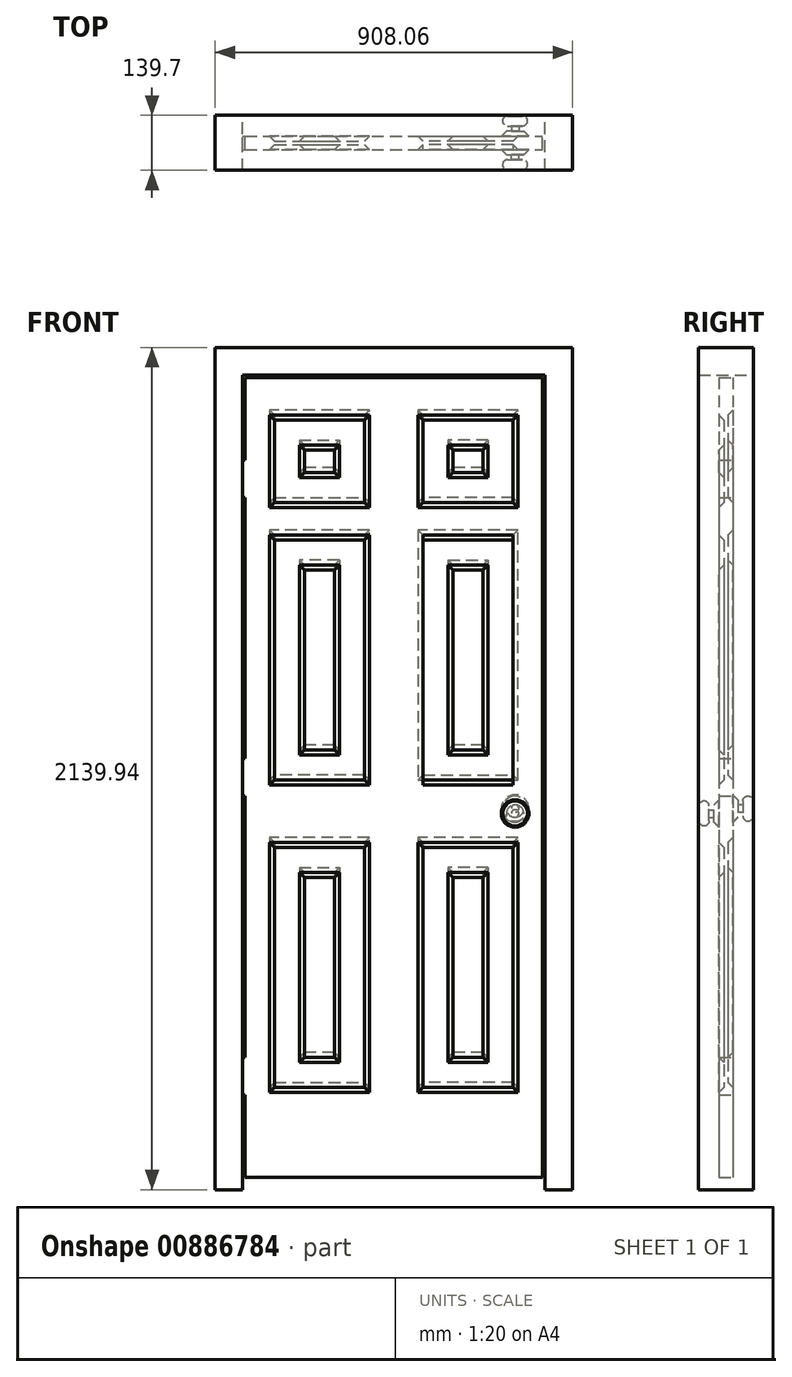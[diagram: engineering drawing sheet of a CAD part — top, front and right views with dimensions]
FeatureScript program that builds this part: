
annotation { "Feature Type Name" : "Feature", "Feature Type Description" : "" }
export const myFeature = defineFeature(function(context is Context, id is Id, definition is map)
    precondition{}
    {
        {
            var Q0;
            Q0=qCreatedBy(makeId("Front.planeOp"),FACE);
            var sketch = newSketch(context, id + "F0", { "sketchPlane" : qUnion([Q0])});
            skLineSegment(sketch, "E0.bottom", {"start": v(-454.03, 1069.98) * mm, "end": v(454.02, 1069.98) * mm});
            skLineSegment(sketch, "E0.top", {"start": v(-454.03, -1069.98) * mm, "end": v(-384.18, -1069.98) * mm});
            skLineSegment(sketch, "E0.left", {"start": v(-454.03, 1069.97) * mm, "end": v(-454.03, -1069.98) * mm});
            skLineSegment(sketch, "E0.right", {"start": v(454.02, 1069.98) * mm, "end": v(454.02, -1069.98) * mm});
            skPoint(sketch, "E0.middle", {"position": v(0, 0) * mm});
            skLineSegment(sketch, "E1.bottom", {"start": v(-384.18, 1000.13) * mm, "end": v(384.17, 1000.13) * mm});
            skLineSegment(sketch, "E1.left", {"start": v(-384.18, 1000.13) * mm, "end": v(-384.18, -1069.98) * mm});
            skLineSegment(sketch, "E1.right", {"start": v(384.17, 1000.13) * mm, "end": v(384.17, -1069.98) * mm});
            skLineSegment(sketch, "E2.trimOffspring", {"start": v(384.17, -1069.98) * mm, "end": v(454.02, -1069.98) * mm});
            skLineSegment(sketch, "E3.bottom", {"start": v(-377.83, 993.78) * mm, "end": v(377.82, 993.78) * mm});
            skLineSegment(sketch, "E3.top", {"start": v(-377.83, -1038.22) * mm, "end": v(377.82, -1038.22) * mm});
            skLineSegment(sketch, "E3.left", {"start": v(-377.83, 993.78) * mm, "end": v(-377.83, 784.23) * mm});
            skLineSegment(sketch, "E3.right", {"start": v(377.82, 993.78) * mm, "end": v(377.82, -1038.22) * mm});
            skLineSegment(sketch, "E4", {"start": v(-384.18, 784.23) * mm, "end": v(-377.83, 784.23) * mm});
            skLineSegment(sketch, "E5", {"start": v(-384.18, 688.98) * mm, "end": v(-377.83, 688.98) * mm});
            skLineSegment(sketch, "E6", {"start": v(-384.18, 25.4) * mm, "end": v(-377.83, 25.4) * mm});
            skLineSegment(sketch, "E7", {"start": v(-384.18, -69.85) * mm, "end": v(-377.83, -69.85) * mm});
            skLineSegment(sketch, "E8", {"start": v(-384.18, -733.42) * mm, "end": v(-377.83, -733.42) * mm});
            skLineSegment(sketch, "E9", {"start": v(-384.18, -828.67) * mm, "end": v(-377.83, -828.67) * mm});
            skLineSegment(sketch, "E10.trimOffspring", {"start": v(-377.83, -828.67) * mm, "end": v(-377.83, -1038.22) * mm});
            skLineSegment(sketch, "E11.trimOffspring", {"start": v(-377.83, -69.85) * mm, "end": v(-377.83, -733.42) * mm});
            skLineSegment(sketch, "E12.trimOffspring", {"start": v(-377.83, 688.98) * mm, "end": v(-377.83, 25.4) * mm});
            skSolve(sketch);
        }
        {
            var Q0;
            Q0=makeQuery(id+"F0.imprint","IMPRINT",FACE,{"disambiguationData":[TD([[makeQuery(id+"F0.imprint","IMPRINT",EDGE,{"derivedFrom":sQuery(id+"F0.wireOp",EDGE,"E0.bottom")}),-1.0]])]});
            extrude(context, id + "F1", {"entities" : qUnion([Q0]), "endBound" : BoundingType.SYMMETRIC, "depth" : 139.7 * mm, "offsetDistance" : 25.4 * mm});
        }
        {
            var Q0;
            Q0=makeQuery(id+"F0.imprint","IMPRINT",FACE,{"disambiguationData":[TD([[makeQuery(id+"F0.imprint","IMPRINT",EDGE,{"derivedFrom":sQuery(id+"F0.wireOp",EDGE,"E3.bottom")}),-1.0]])]});
            extrude(context, id + "F2", {"entities" : qUnion([Q0]), "operationType" : NewBodyOperationType.ADD, "endBound" : BoundingType.SYMMETRIC, "depth" : 34.92 * mm, "offsetDistance" : 25.4 * mm});
        }
        {
            var Q0;
            Q0=makeQuery(id+"F2.opExtrude","CAP_FACE",FACE,{"disambiguationData":[OSD([sQuery(id+"F0.wireOp",EDGE,"E1.left"),sQuery(id+"F0.wireOp",EDGE,"E3.bottom"),sQuery(id+"F0.wireOp",EDGE,"E3.top"),sQuery(id+"F0.wireOp",EDGE,"E3.left"),sQuery(id+"F0.wireOp",EDGE,"E3.right"),sQuery(id+"F0.wireOp",EDGE,"E4"),sQuery(id+"F0.wireOp",EDGE,"E5"),sQuery(id+"F0.wireOp",EDGE,"E6"),sQuery(id+"F0.wireOp",EDGE,"E7"),sQuery(id+"F0.wireOp",EDGE,"E8"),sQuery(id+"F0.wireOp",EDGE,"E9"),sQuery(id+"F0.wireOp",EDGE,"E10.trimOffspring"),sQuery(id+"F0.wireOp",EDGE,"E11.trimOffspring"),sQuery(id+"F0.wireOp",EDGE,"E12.trimOffspring")])],"isStart":false});
            var sketch = newSketch(context, id + "F3", { "sketchPlane" : qUnion([Q0])});
            skLineSegment(sketch, "E13", {"start": v(0, 520.5) * mm, "end": v(0, -306.5) * mm});
            skLineSegment(sketch, "E14.bottom", {"start": v(-303.21, 885.83) * mm, "end": v(-74.61, 885.83) * mm});
            skLineSegment(sketch, "E14.top", {"start": v(-303.21, 676.28) * mm, "end": v(-74.61, 676.28) * mm});
            skLineSegment(sketch, "E14.left", {"start": v(-303.21, 885.83) * mm, "end": v(-303.21, 676.28) * mm});
            skLineSegment(sketch, "E14.right", {"start": v(-74.61, 885.83) * mm, "end": v(-74.61, 676.28) * mm});
            skLineSegment(sketch, "E15.bottom", {"start": v(-74.61, 581.03) * mm, "end": v(-303.21, 581.03) * mm});
            skLineSegment(sketch, "E15.top", {"start": v(-74.61, -28.57) * mm, "end": v(-303.21, -28.57) * mm});
            skLineSegment(sketch, "E15.left", {"start": v(-74.61, 581.03) * mm, "end": v(-74.61, -28.57) * mm});
            skLineSegment(sketch, "E15.right", {"start": v(-303.21, 581.03) * mm, "end": v(-303.21, -28.57) * mm});
            skLineSegment(sketch, "E16.bottom", {"start": v(-303.21, -200.02) * mm, "end": v(-74.61, -200.02) * mm});
            skLineSegment(sketch, "E16.top", {"start": v(-303.21, -809.62) * mm, "end": v(-74.61, -809.62) * mm});
            skLineSegment(sketch, "E16.left", {"start": v(-303.21, -200.02) * mm, "end": v(-303.21, -809.62) * mm});
            skLineSegment(sketch, "E16.right", {"start": v(-74.61, -200.02) * mm, "end": v(-74.61, -809.62) * mm});
            skLineSegment(sketch, "E17.0", {"start": v(-239.71, -263.52) * mm, "end": v(-239.71, -746.12) * mm});
            skLineSegment(sketch, "E17.1", {"start": v(-239.71, -263.52) * mm, "end": v(-138.11, -263.52) * mm});
            skLineSegment(sketch, "E17.2", {"start": v(-138.11, -263.52) * mm, "end": v(-138.11, -746.12) * mm});
            skLineSegment(sketch, "E17.3", {"start": v(-239.71, -746.12) * mm, "end": v(-138.11, -746.12) * mm});
            skLineSegment(sketch, "E18.0", {"start": v(-239.71, 517.53) * mm, "end": v(-239.71, 34.93) * mm});
            skLineSegment(sketch, "E18.1", {"start": v(-138.11, 517.53) * mm, "end": v(-239.71, 517.53) * mm});
            skLineSegment(sketch, "E18.2", {"start": v(-138.11, 517.53) * mm, "end": v(-138.11, 34.93) * mm});
            skLineSegment(sketch, "E18.3", {"start": v(-138.11, 34.93) * mm, "end": v(-239.71, 34.93) * mm});
            skLineSegment(sketch, "E19.0", {"start": v(-239.71, 822.33) * mm, "end": v(-239.71, 739.78) * mm});
            skLineSegment(sketch, "E19.1", {"start": v(-239.71, 822.33) * mm, "end": v(-138.11, 822.33) * mm});
            skLineSegment(sketch, "E19.2", {"start": v(-138.11, 822.33) * mm, "end": v(-138.11, 739.78) * mm});
            skLineSegment(sketch, "E19.3", {"start": v(-239.71, 739.78) * mm, "end": v(-138.11, 739.78) * mm});
            skLineSegment(sketch, "E20.MirrorCS", {"start": v(239.71, 822.33) * mm, "end": v(239.71, 739.78) * mm});
            skLineSegment(sketch, "E21.MirrorCS", {"start": v(138.11, 822.33) * mm, "end": v(138.11, 739.78) * mm});
            skLineSegment(sketch, "E22.MirrorCS", {"start": v(74.61, 885.83) * mm, "end": v(74.61, 676.28) * mm});
            skLineSegment(sketch, "E23.MirrorCS", {"start": v(303.21, 885.83) * mm, "end": v(74.61, 885.83) * mm});
            skLineSegment(sketch, "E24.MirrorCS", {"start": v(303.21, 676.28) * mm, "end": v(74.61, 676.28) * mm});
            skLineSegment(sketch, "E25.MirrorCS", {"start": v(303.21, 581.03) * mm, "end": v(303.21, -28.57) * mm});
            skLineSegment(sketch, "E26.MirrorCS", {"start": v(239.71, 517.53) * mm, "end": v(239.71, 34.93) * mm});
            skLineSegment(sketch, "E27.MirrorCS", {"start": v(138.11, 34.93) * mm, "end": v(239.71, 34.93) * mm});
            skLineSegment(sketch, "E28.MirrorCS", {"start": v(74.61, 581.03) * mm, "end": v(74.61, -28.57) * mm});
            skLineSegment(sketch, "E29.MirrorCS", {"start": v(303.21, -809.62) * mm, "end": v(74.61, -809.62) * mm});
            skLineSegment(sketch, "E30.MirrorCS", {"start": v(138.11, 517.53) * mm, "end": v(239.71, 517.53) * mm});
            skLineSegment(sketch, "E31.MirrorCS", {"start": v(74.61, -28.57) * mm, "end": v(303.21, -28.57) * mm});
            skLineSegment(sketch, "E32.MirrorCS", {"start": v(239.71, 822.33) * mm, "end": v(138.11, 822.33) * mm});
            skLineSegment(sketch, "E33.MirrorCS", {"start": v(239.71, -263.52) * mm, "end": v(138.11, -263.52) * mm});
            skLineSegment(sketch, "E34.MirrorCS", {"start": v(239.71, 739.78) * mm, "end": v(138.11, 739.78) * mm});
            skLineSegment(sketch, "E35.MirrorCS", {"start": v(303.21, 885.83) * mm, "end": v(303.21, 676.28) * mm});
            skLineSegment(sketch, "E36.MirrorCS", {"start": v(303.21, -200.02) * mm, "end": v(74.61, -200.02) * mm});
            skLineSegment(sketch, "E37.MirrorCS", {"start": v(138.11, 517.53) * mm, "end": v(138.11, 34.93) * mm});
            skLineSegment(sketch, "E38.MirrorCS", {"start": v(239.71, -746.12) * mm, "end": v(138.11, -746.12) * mm});
            skLineSegment(sketch, "E39.MirrorCS", {"start": v(138.11, -263.52) * mm, "end": v(138.11, -746.12) * mm});
            skLineSegment(sketch, "E40.MirrorCS", {"start": v(303.21, -200.02) * mm, "end": v(303.21, -809.62) * mm});
            skLineSegment(sketch, "E41.MirrorCS", {"start": v(74.61, 581.03) * mm, "end": v(303.21, 581.03) * mm});
            skLineSegment(sketch, "E42.MirrorCS", {"start": v(74.61, -200.02) * mm, "end": v(74.61, -809.62) * mm});
            skLineSegment(sketch, "E43.MirrorCS", {"start": v(239.71, -263.52) * mm, "end": v(239.71, -746.12) * mm});
            skSolve(sketch);
        }
        {
            var Q0;
            Q0=makeQuery(id+"F3.imprint","IMPRINT",FACE,{"disambiguationData":[TD([[makeQuery(id+"F3.imprint","IMPRINT",EDGE,{"derivedFrom":sQuery(id+"F3.wireOp",EDGE,"E14.bottom")}),-1.0]])]});
            var Q1;
            Q1=makeQuery(id+"F3.imprint","IMPRINT",FACE,{"disambiguationData":[TD([[makeQuery(id+"F3.imprint","IMPRINT",EDGE,{"derivedFrom":sQuery(id+"F3.wireOp",EDGE,"E15.bottom")}),1.0]])]});
            var Q2;
            Q2=makeQuery(id+"F3.imprint","IMPRINT",FACE,{"disambiguationData":[TD([[makeQuery(id+"F3.imprint","IMPRINT",EDGE,{"derivedFrom":sQuery(id+"F3.wireOp",EDGE,"E20.MirrorCS")}),1.0]])]});
            var Q3;
            Q3=makeQuery(id+"F3.imprint","IMPRINT",FACE,{"disambiguationData":[TD([[makeQuery(id+"F3.imprint","IMPRINT",EDGE,{"derivedFrom":sQuery(id+"F3.wireOp",EDGE,"E25.MirrorCS")}),-1.0]])]});
            var Q4;
            Q4=makeQuery(id+"F3.imprint","IMPRINT",FACE,{"disambiguationData":[TD([[makeQuery(id+"F3.imprint","IMPRINT",EDGE,{"derivedFrom":sQuery(id+"F3.wireOp",EDGE,"E16.bottom")}),-1.0]])]});
            var Q5;
            Q5=makeQuery(id+"F3.imprint","IMPRINT",FACE,{"disambiguationData":[TD([[makeQuery(id+"F3.imprint","IMPRINT",EDGE,{"derivedFrom":sQuery(id+"F3.wireOp",EDGE,"E29.MirrorCS")}),-1.0]])]});
            extrude(context, id + "F4", {"entities" : qUnion([Q0, Q1, Q2, Q3, Q4, Q5]), "operationType" : NewBodyOperationType.REMOVE, "oppositeDirection" : true, "depth" : 12.7 * mm, "offsetDistance" : 25.4 * mm});
        }
        {
            var Q0;
            Q0=makeQuery(id+"F4.boolean.opBoolean","SPLIT",FACE,{"disambiguationData":[TD([makeQuery(id+"F4.opExtrude","SWEPT_FACE",FACE,{"disambiguationData":[OSD([sQuery(id+"F3.wireOp",EDGE,"E18.0")])]})])],"derivedFrom":makeQuery(id+"F2.opExtrude","CAP_FACE",FACE,{"disambiguationData":[OSD([sQuery(id+"F0.wireOp",EDGE,"E1.left"),sQuery(id+"F0.wireOp",EDGE,"E3.bottom"),sQuery(id+"F0.wireOp",EDGE,"E3.top"),sQuery(id+"F0.wireOp",EDGE,"E3.left"),sQuery(id+"F0.wireOp",EDGE,"E3.right"),sQuery(id+"F0.wireOp",EDGE,"E4"),sQuery(id+"F0.wireOp",EDGE,"E5"),sQuery(id+"F0.wireOp",EDGE,"E6"),sQuery(id+"F0.wireOp",EDGE,"E7"),sQuery(id+"F0.wireOp",EDGE,"E8"),sQuery(id+"F0.wireOp",EDGE,"E9"),sQuery(id+"F0.wireOp",EDGE,"E10.trimOffspring"),sQuery(id+"F0.wireOp",EDGE,"E11.trimOffspring"),sQuery(id+"F0.wireOp",EDGE,"E12.trimOffspring")])],"isStart":false})});
            var Q1;
            Q1=makeQuery(id+"F4.boolean.opBoolean","SPLIT",FACE,{"disambiguationData":[TD([makeQuery(id+"F4.opExtrude","SWEPT_FACE",FACE,{"disambiguationData":[OSD([sQuery(id+"F3.wireOp",EDGE,"E19.0")])]})])],"derivedFrom":makeQuery(id+"F2.opExtrude","CAP_FACE",FACE,{"disambiguationData":[OSD([sQuery(id+"F0.wireOp",EDGE,"E1.left"),sQuery(id+"F0.wireOp",EDGE,"E3.bottom"),sQuery(id+"F0.wireOp",EDGE,"E3.top"),sQuery(id+"F0.wireOp",EDGE,"E3.left"),sQuery(id+"F0.wireOp",EDGE,"E3.right"),sQuery(id+"F0.wireOp",EDGE,"E4"),sQuery(id+"F0.wireOp",EDGE,"E5"),sQuery(id+"F0.wireOp",EDGE,"E6"),sQuery(id+"F0.wireOp",EDGE,"E7"),sQuery(id+"F0.wireOp",EDGE,"E8"),sQuery(id+"F0.wireOp",EDGE,"E9"),sQuery(id+"F0.wireOp",EDGE,"E10.trimOffspring"),sQuery(id+"F0.wireOp",EDGE,"E11.trimOffspring"),sQuery(id+"F0.wireOp",EDGE,"E12.trimOffspring")])],"isStart":false})});
            var Q2;
            Q2=makeQuery(id+"F4.boolean.opBoolean","SPLIT",FACE,{"disambiguationData":[TD([makeQuery(id+"F4.opExtrude","SWEPT_FACE",FACE,{"disambiguationData":[OSD([sQuery(id+"F3.wireOp",EDGE,"E20.MirrorCS")])]})])],"derivedFrom":makeQuery(id+"F2.opExtrude","CAP_FACE",FACE,{"disambiguationData":[OSD([sQuery(id+"F0.wireOp",EDGE,"E1.left"),sQuery(id+"F0.wireOp",EDGE,"E3.bottom"),sQuery(id+"F0.wireOp",EDGE,"E3.top"),sQuery(id+"F0.wireOp",EDGE,"E3.left"),sQuery(id+"F0.wireOp",EDGE,"E3.right"),sQuery(id+"F0.wireOp",EDGE,"E4"),sQuery(id+"F0.wireOp",EDGE,"E5"),sQuery(id+"F0.wireOp",EDGE,"E6"),sQuery(id+"F0.wireOp",EDGE,"E7"),sQuery(id+"F0.wireOp",EDGE,"E8"),sQuery(id+"F0.wireOp",EDGE,"E9"),sQuery(id+"F0.wireOp",EDGE,"E10.trimOffspring"),sQuery(id+"F0.wireOp",EDGE,"E11.trimOffspring"),sQuery(id+"F0.wireOp",EDGE,"E12.trimOffspring")])],"isStart":false})});
            var Q3;
            Q3=makeQuery(id+"F4.boolean.opBoolean","SPLIT",FACE,{"disambiguationData":[TD([makeQuery(id+"F4.opExtrude","SWEPT_FACE",FACE,{"disambiguationData":[OSD([sQuery(id+"F3.wireOp",EDGE,"E26.MirrorCS")])]})])],"derivedFrom":makeQuery(id+"F2.opExtrude","CAP_FACE",FACE,{"disambiguationData":[OSD([sQuery(id+"F0.wireOp",EDGE,"E1.left"),sQuery(id+"F0.wireOp",EDGE,"E3.bottom"),sQuery(id+"F0.wireOp",EDGE,"E3.top"),sQuery(id+"F0.wireOp",EDGE,"E3.left"),sQuery(id+"F0.wireOp",EDGE,"E3.right"),sQuery(id+"F0.wireOp",EDGE,"E4"),sQuery(id+"F0.wireOp",EDGE,"E5"),sQuery(id+"F0.wireOp",EDGE,"E6"),sQuery(id+"F0.wireOp",EDGE,"E7"),sQuery(id+"F0.wireOp",EDGE,"E8"),sQuery(id+"F0.wireOp",EDGE,"E9"),sQuery(id+"F0.wireOp",EDGE,"E10.trimOffspring"),sQuery(id+"F0.wireOp",EDGE,"E11.trimOffspring"),sQuery(id+"F0.wireOp",EDGE,"E12.trimOffspring")])],"isStart":false})});
            var Q4;
            Q4=makeQuery(id+"F4.boolean.opBoolean","SPLIT",FACE,{"disambiguationData":[TD([makeQuery(id+"F4.opExtrude","SWEPT_FACE",FACE,{"disambiguationData":[OSD([sQuery(id+"F3.wireOp",EDGE,"E17.0")])]})])],"derivedFrom":makeQuery(id+"F2.opExtrude","CAP_FACE",FACE,{"disambiguationData":[OSD([sQuery(id+"F0.wireOp",EDGE,"E1.left"),sQuery(id+"F0.wireOp",EDGE,"E3.bottom"),sQuery(id+"F0.wireOp",EDGE,"E3.top"),sQuery(id+"F0.wireOp",EDGE,"E3.left"),sQuery(id+"F0.wireOp",EDGE,"E3.right"),sQuery(id+"F0.wireOp",EDGE,"E4"),sQuery(id+"F0.wireOp",EDGE,"E5"),sQuery(id+"F0.wireOp",EDGE,"E6"),sQuery(id+"F0.wireOp",EDGE,"E7"),sQuery(id+"F0.wireOp",EDGE,"E8"),sQuery(id+"F0.wireOp",EDGE,"E9"),sQuery(id+"F0.wireOp",EDGE,"E10.trimOffspring"),sQuery(id+"F0.wireOp",EDGE,"E11.trimOffspring"),sQuery(id+"F0.wireOp",EDGE,"E12.trimOffspring")])],"isStart":false})});
            var Q5;
            Q5=makeQuery(id+"F4.boolean.opBoolean","SPLIT",FACE,{"disambiguationData":[TD([makeQuery(id+"F4.opExtrude","SWEPT_FACE",FACE,{"disambiguationData":[OSD([sQuery(id+"F3.wireOp",EDGE,"E33.MirrorCS")])]})])],"derivedFrom":makeQuery(id+"F2.opExtrude","CAP_FACE",FACE,{"disambiguationData":[OSD([sQuery(id+"F0.wireOp",EDGE,"E1.left"),sQuery(id+"F0.wireOp",EDGE,"E3.bottom"),sQuery(id+"F0.wireOp",EDGE,"E3.top"),sQuery(id+"F0.wireOp",EDGE,"E3.left"),sQuery(id+"F0.wireOp",EDGE,"E3.right"),sQuery(id+"F0.wireOp",EDGE,"E4"),sQuery(id+"F0.wireOp",EDGE,"E5"),sQuery(id+"F0.wireOp",EDGE,"E6"),sQuery(id+"F0.wireOp",EDGE,"E7"),sQuery(id+"F0.wireOp",EDGE,"E8"),sQuery(id+"F0.wireOp",EDGE,"E9"),sQuery(id+"F0.wireOp",EDGE,"E10.trimOffspring"),sQuery(id+"F0.wireOp",EDGE,"E11.trimOffspring"),sQuery(id+"F0.wireOp",EDGE,"E12.trimOffspring")])],"isStart":false})});
            var Q6;
            Q6=makeQuery(id+"F4.boolean.opBoolean","COPY",EDGE,{"derivedFrom":makeQuery(id+"F4.opExtrude","CAP_EDGE",EDGE,{"disambiguationData":[OSD([sQuery(id+"F3.wireOp",EDGE,"E14.left")])],"isStart":true})});
            var Q7;
            Q7=makeQuery(id+"F4.boolean.opBoolean","COPY",EDGE,{"derivedFrom":makeQuery(id+"F4.opExtrude","CAP_EDGE",EDGE,{"disambiguationData":[OSD([sQuery(id+"F3.wireOp",EDGE,"E14.bottom")])],"isStart":true})});
            var Q8;
            Q8=makeQuery(id+"F4.boolean.opBoolean","COPY",EDGE,{"derivedFrom":makeQuery(id+"F4.opExtrude","CAP_EDGE",EDGE,{"disambiguationData":[OSD([sQuery(id+"F3.wireOp",EDGE,"E14.right")])],"isStart":true})});
            var Q9;
            Q9=makeQuery(id+"F4.boolean.opBoolean","COPY",EDGE,{"derivedFrom":makeQuery(id+"F4.opExtrude","CAP_EDGE",EDGE,{"disambiguationData":[OSD([sQuery(id+"F3.wireOp",EDGE,"E14.top")])],"isStart":true})});
            var Q10;
            Q10=makeQuery(id+"F4.boolean.opBoolean","COPY",EDGE,{"derivedFrom":makeQuery(id+"F4.opExtrude","CAP_EDGE",EDGE,{"disambiguationData":[OSD([sQuery(id+"F3.wireOp",EDGE,"E15.bottom")])],"isStart":true})});
            var Q11;
            Q11=makeQuery(id+"F4.boolean.opBoolean","COPY",EDGE,{"derivedFrom":makeQuery(id+"F4.opExtrude","CAP_EDGE",EDGE,{"disambiguationData":[OSD([sQuery(id+"F3.wireOp",EDGE,"E15.right")])],"isStart":true})});
            var Q12;
            Q12=makeQuery(id+"F4.boolean.opBoolean","COPY",EDGE,{"derivedFrom":makeQuery(id+"F4.opExtrude","CAP_EDGE",EDGE,{"disambiguationData":[OSD([sQuery(id+"F3.wireOp",EDGE,"E15.left")])],"isStart":true})});
            var Q13;
            Q13=makeQuery(id+"F4.boolean.opBoolean","COPY",EDGE,{"derivedFrom":makeQuery(id+"F4.opExtrude","CAP_EDGE",EDGE,{"disambiguationData":[OSD([sQuery(id+"F3.wireOp",EDGE,"E22.MirrorCS")])],"isStart":true})});
            var Q14;
            Q14=makeQuery(id+"F4.boolean.opBoolean","COPY",EDGE,{"derivedFrom":makeQuery(id+"F4.opExtrude","CAP_EDGE",EDGE,{"disambiguationData":[OSD([sQuery(id+"F3.wireOp",EDGE,"E23.MirrorCS")])],"isStart":true})});
            var Q15;
            Q15=makeQuery(id+"F4.boolean.opBoolean","COPY",EDGE,{"derivedFrom":makeQuery(id+"F4.opExtrude","CAP_EDGE",EDGE,{"disambiguationData":[OSD([sQuery(id+"F3.wireOp",EDGE,"E35.MirrorCS")])],"isStart":true})});
            var Q16;
            Q16=makeQuery(id+"F4.boolean.opBoolean","COPY",EDGE,{"derivedFrom":makeQuery(id+"F4.opExtrude","CAP_EDGE",EDGE,{"disambiguationData":[OSD([sQuery(id+"F3.wireOp",EDGE,"E24.MirrorCS")])],"isStart":true})});
            var Q17;
            Q17=makeQuery(id+"F4.boolean.opBoolean","COPY",EDGE,{"derivedFrom":makeQuery(id+"F4.opExtrude","CAP_EDGE",EDGE,{"disambiguationData":[OSD([sQuery(id+"F3.wireOp",EDGE,"E41.MirrorCS")])],"isStart":true})});
            var Q18;
            Q18=makeQuery(id+"F4.boolean.opBoolean","COPY",EDGE,{"derivedFrom":makeQuery(id+"F4.opExtrude","CAP_EDGE",EDGE,{"disambiguationData":[OSD([sQuery(id+"F3.wireOp",EDGE,"E15.top")])],"isStart":true})});
            var Q19;
            Q19=makeQuery(id+"F4.boolean.opBoolean","COPY",EDGE,{"derivedFrom":makeQuery(id+"F4.opExtrude","CAP_EDGE",EDGE,{"disambiguationData":[OSD([sQuery(id+"F3.wireOp",EDGE,"E31.MirrorCS")])],"isStart":true})});
            var Q20;
            Q20=makeQuery(id+"F4.boolean.opBoolean","COPY",EDGE,{"derivedFrom":makeQuery(id+"F4.opExtrude","CAP_EDGE",EDGE,{"disambiguationData":[OSD([sQuery(id+"F3.wireOp",EDGE,"E16.bottom")])],"isStart":true})});
            var Q21;
            Q21=makeQuery(id+"F4.boolean.opBoolean","COPY",EDGE,{"derivedFrom":makeQuery(id+"F4.opExtrude","CAP_EDGE",EDGE,{"disambiguationData":[OSD([sQuery(id+"F3.wireOp",EDGE,"E16.left")])],"isStart":true})});
            var Q22;
            Q22=makeQuery(id+"F4.boolean.opBoolean","COPY",EDGE,{"derivedFrom":makeQuery(id+"F4.opExtrude","CAP_EDGE",EDGE,{"disambiguationData":[OSD([sQuery(id+"F3.wireOp",EDGE,"E16.right")])],"isStart":true})});
            var Q23;
            Q23=makeQuery(id+"F4.boolean.opBoolean","COPY",EDGE,{"derivedFrom":makeQuery(id+"F4.opExtrude","CAP_EDGE",EDGE,{"disambiguationData":[OSD([sQuery(id+"F3.wireOp",EDGE,"E36.MirrorCS")])],"isStart":true})});
            var Q24;
            Q24=makeQuery(id+"F4.boolean.opBoolean","COPY",EDGE,{"derivedFrom":makeQuery(id+"F4.opExtrude","CAP_EDGE",EDGE,{"disambiguationData":[OSD([sQuery(id+"F3.wireOp",EDGE,"E42.MirrorCS")])],"isStart":true})});
            var Q25;
            Q25=makeQuery(id+"F4.boolean.opBoolean","COPY",EDGE,{"derivedFrom":makeQuery(id+"F4.opExtrude","CAP_EDGE",EDGE,{"disambiguationData":[OSD([sQuery(id+"F3.wireOp",EDGE,"E40.MirrorCS")])],"isStart":true})});
            var Q26;
            Q26=makeQuery(id+"F4.boolean.opBoolean","COPY",EDGE,{"derivedFrom":makeQuery(id+"F4.opExtrude","CAP_EDGE",EDGE,{"disambiguationData":[OSD([sQuery(id+"F3.wireOp",EDGE,"E16.top")])],"isStart":true})});
            var Q27;
            Q27=makeQuery(id+"F4.boolean.opBoolean","COPY",EDGE,{"derivedFrom":makeQuery(id+"F4.opExtrude","CAP_EDGE",EDGE,{"disambiguationData":[OSD([sQuery(id+"F3.wireOp",EDGE,"E29.MirrorCS")])],"isStart":true})});
            chamfer(context, id + "F5", {"entities" : qUnion([Q0, Q1, Q2, Q3, Q4, Q5, Q6, Q7, Q8, Q9, Q10, Q11, Q12, Q13, Q14, Q15, Q16, Q17, Q18, Q19, Q20, Q21, Q22, Q23, Q24, Q25, Q26, Q27]), "width" : 12.7 * mm, "tangentPropagation" : true});
        }
        {
            var Q0;
            Q0=makeQuery(id+"F2.opExtrude","CAP_FACE",FACE,{"disambiguationData":[OSD([sQuery(id+"F0.wireOp",EDGE,"E1.left"),sQuery(id+"F0.wireOp",EDGE,"E3.bottom"),sQuery(id+"F0.wireOp",EDGE,"E3.top"),sQuery(id+"F0.wireOp",EDGE,"E3.left"),sQuery(id+"F0.wireOp",EDGE,"E3.right"),sQuery(id+"F0.wireOp",EDGE,"E4"),sQuery(id+"F0.wireOp",EDGE,"E5"),sQuery(id+"F0.wireOp",EDGE,"E6"),sQuery(id+"F0.wireOp",EDGE,"E7"),sQuery(id+"F0.wireOp",EDGE,"E8"),sQuery(id+"F0.wireOp",EDGE,"E9"),sQuery(id+"F0.wireOp",EDGE,"E10.trimOffspring"),sQuery(id+"F0.wireOp",EDGE,"E11.trimOffspring"),sQuery(id+"F0.wireOp",EDGE,"E12.trimOffspring")])],"isStart":true});
            var sketch = newSketch(context, id + "F6", { "sketchPlane" : qUnion([Q0])});
            skLineSegment(sketch, "E44", {"start": v(0.45, 315.7) * mm, "end": v(0.45, -511.3) * mm});
            skLineSegment(sketch, "E45.bottom", {"start": v(-302.76, 898.53) * mm, "end": v(-74.16, 898.53) * mm});
            skLineSegment(sketch, "E45.top", {"start": v(-302.76, 688.98) * mm, "end": v(-74.16, 688.98) * mm});
            skLineSegment(sketch, "E45.left", {"start": v(-302.76, 898.53) * mm, "end": v(-302.76, 688.98) * mm});
            skLineSegment(sketch, "E45.right", {"start": v(-74.16, 898.53) * mm, "end": v(-74.16, 688.98) * mm});
            skLineSegment(sketch, "E46.bottom", {"start": v(-74.16, 593.73) * mm, "end": v(-302.76, 593.73) * mm});
            skLineSegment(sketch, "E46.top", {"start": v(-74.16, -15.87) * mm, "end": v(-302.76, -15.87) * mm});
            skLineSegment(sketch, "E46.left", {"start": v(-74.16, 593.73) * mm, "end": v(-74.16, -15.87) * mm});
            skLineSegment(sketch, "E46.right", {"start": v(-302.76, 593.73) * mm, "end": v(-302.76, -15.87) * mm});
            skLineSegment(sketch, "E47.bottom", {"start": v(-302.76, -187.32) * mm, "end": v(-74.16, -187.32) * mm});
            skLineSegment(sketch, "E47.top", {"start": v(-302.76, -796.92) * mm, "end": v(-74.16, -796.92) * mm});
            skLineSegment(sketch, "E47.left", {"start": v(-302.76, -187.32) * mm, "end": v(-302.76, -796.92) * mm});
            skLineSegment(sketch, "E47.right", {"start": v(-74.16, -187.32) * mm, "end": v(-74.16, -796.92) * mm});
            skLineSegment(sketch, "E48.0", {"start": v(-239.26, -250.82) * mm, "end": v(-239.26, -733.42) * mm});
            skLineSegment(sketch, "E48.1", {"start": v(-239.26, -250.82) * mm, "end": v(-137.66, -250.82) * mm});
            skLineSegment(sketch, "E48.2", {"start": v(-137.66, -250.82) * mm, "end": v(-137.66, -733.42) * mm});
            skLineSegment(sketch, "E48.3", {"start": v(-239.26, -733.42) * mm, "end": v(-137.66, -733.42) * mm});
            skLineSegment(sketch, "E49.0", {"start": v(-239.26, 530.23) * mm, "end": v(-239.26, 47.63) * mm});
            skLineSegment(sketch, "E49.1", {"start": v(-137.66, 530.23) * mm, "end": v(-239.26, 530.23) * mm});
            skLineSegment(sketch, "E49.2", {"start": v(-137.66, 530.23) * mm, "end": v(-137.66, 47.63) * mm});
            skLineSegment(sketch, "E49.3", {"start": v(-137.66, 47.63) * mm, "end": v(-239.26, 47.63) * mm});
            skLineSegment(sketch, "E50.0", {"start": v(-239.26, 835.03) * mm, "end": v(-239.26, 752.48) * mm});
            skLineSegment(sketch, "E50.1", {"start": v(-239.26, 835.03) * mm, "end": v(-137.66, 835.03) * mm});
            skLineSegment(sketch, "E50.2", {"start": v(-137.66, 835.03) * mm, "end": v(-137.66, 752.48) * mm});
            skLineSegment(sketch, "E50.3", {"start": v(-239.26, 752.48) * mm, "end": v(-137.66, 752.48) * mm});
            skLineSegment(sketch, "E51.MirrorCS", {"start": v(240.16, 835.03) * mm, "end": v(240.16, 752.48) * mm});
            skLineSegment(sketch, "E52.MirrorCS", {"start": v(138.56, 835.03) * mm, "end": v(138.56, 752.48) * mm});
            skLineSegment(sketch, "E53.MirrorCS", {"start": v(75.06, 898.53) * mm, "end": v(75.06, 688.98) * mm});
            skLineSegment(sketch, "E54.MirrorCS", {"start": v(303.66, 898.53) * mm, "end": v(75.06, 898.53) * mm});
            skLineSegment(sketch, "E55.MirrorCS", {"start": v(303.66, 688.98) * mm, "end": v(75.06, 688.98) * mm});
            skLineSegment(sketch, "E56.MirrorCS", {"start": v(303.66, 593.73) * mm, "end": v(303.66, -15.87) * mm});
            skLineSegment(sketch, "E57.MirrorCS", {"start": v(240.16, 530.23) * mm, "end": v(240.16, 47.63) * mm});
            skLineSegment(sketch, "E58.MirrorCS", {"start": v(138.56, 47.63) * mm, "end": v(240.16, 47.63) * mm});
            skLineSegment(sketch, "E59.MirrorCS", {"start": v(75.06, 593.73) * mm, "end": v(75.06, -15.87) * mm});
            skLineSegment(sketch, "E60.MirrorCS", {"start": v(303.66, -796.92) * mm, "end": v(75.06, -796.92) * mm});
            skLineSegment(sketch, "E61.MirrorCS", {"start": v(138.56, 530.23) * mm, "end": v(240.16, 530.23) * mm});
            skLineSegment(sketch, "E62.MirrorCS", {"start": v(75.06, -15.87) * mm, "end": v(303.66, -15.87) * mm});
            skLineSegment(sketch, "E63.MirrorCS", {"start": v(240.16, 835.03) * mm, "end": v(138.56, 835.03) * mm});
            skLineSegment(sketch, "E64.MirrorCS", {"start": v(240.16, -250.82) * mm, "end": v(138.56, -250.82) * mm});
            skLineSegment(sketch, "E65.MirrorCS", {"start": v(240.16, 752.48) * mm, "end": v(138.56, 752.48) * mm});
            skLineSegment(sketch, "E66.MirrorCS", {"start": v(303.66, 898.53) * mm, "end": v(303.66, 688.98) * mm});
            skLineSegment(sketch, "E67.MirrorCS", {"start": v(303.66, -187.32) * mm, "end": v(75.06, -187.32) * mm});
            skLineSegment(sketch, "E68.MirrorCS", {"start": v(138.56, 530.23) * mm, "end": v(138.56, 47.63) * mm});
            skLineSegment(sketch, "E69.MirrorCS", {"start": v(240.16, -733.42) * mm, "end": v(138.56, -733.42) * mm});
            skLineSegment(sketch, "E70.MirrorCS", {"start": v(138.56, -250.82) * mm, "end": v(138.56, -733.42) * mm});
            skLineSegment(sketch, "E71.MirrorCS", {"start": v(303.66, -187.32) * mm, "end": v(303.66, -796.92) * mm});
            skLineSegment(sketch, "E72.MirrorCS", {"start": v(75.06, 593.73) * mm, "end": v(303.66, 593.73) * mm});
            skLineSegment(sketch, "E73.MirrorCS", {"start": v(75.06, -187.32) * mm, "end": v(75.06, -796.92) * mm});
            skLineSegment(sketch, "E74.MirrorCS", {"start": v(240.16, -250.82) * mm, "end": v(240.16, -733.42) * mm});
            skSolve(sketch);
        }
        {
            var Q0;
            Q0=makeQuery(id+"F6.imprint","IMPRINT",FACE,{"disambiguationData":[TD([[makeQuery(id+"F6.imprint","IMPRINT",EDGE,{"derivedFrom":sQuery(id+"F6.wireOp",EDGE,"E45.bottom")}),-1.0]])]});
            var Q1;
            Q1=makeQuery(id+"F6.imprint","IMPRINT",FACE,{"disambiguationData":[TD([[makeQuery(id+"F6.imprint","IMPRINT",EDGE,{"derivedFrom":sQuery(id+"F6.wireOp",EDGE,"E51.MirrorCS")}),1.0]])]});
            var Q2;
            Q2=makeQuery(id+"F6.imprint","IMPRINT",FACE,{"disambiguationData":[TD([[makeQuery(id+"F6.imprint","IMPRINT",EDGE,{"derivedFrom":sQuery(id+"F6.wireOp",EDGE,"E46.bottom")}),1.0]])]});
            var Q3;
            Q3=makeQuery(id+"F6.imprint","IMPRINT",FACE,{"disambiguationData":[TD([[makeQuery(id+"F6.imprint","IMPRINT",EDGE,{"derivedFrom":sQuery(id+"F6.wireOp",EDGE,"E56.MirrorCS")}),-1.0]])]});
            var Q4;
            Q4=makeQuery(id+"F6.imprint","IMPRINT",FACE,{"disambiguationData":[TD([[makeQuery(id+"F6.imprint","IMPRINT",EDGE,{"derivedFrom":sQuery(id+"F6.wireOp",EDGE,"E60.MirrorCS")}),-1.0]])]});
            var Q5;
            Q5=makeQuery(id+"F6.imprint","IMPRINT",FACE,{"disambiguationData":[TD([[makeQuery(id+"F6.imprint","IMPRINT",EDGE,{"derivedFrom":sQuery(id+"F6.wireOp",EDGE,"E47.bottom")}),-1.0]])]});
            extrude(context, id + "F7", {"entities" : qUnion([Q0, Q1, Q2, Q3, Q4, Q5]), "operationType" : NewBodyOperationType.REMOVE, "oppositeDirection" : true, "depth" : 12.7 * mm, "offsetDistance" : 25.4 * mm});
        }
        {
            var Q0;
            Q0=makeQuery(id+"F7.boolean.opBoolean","SPLIT",FACE,{"disambiguationData":[TD([makeQuery(id+"F7.opExtrude","SWEPT_FACE",FACE,{"disambiguationData":[OSD([sQuery(id+"F6.wireOp",EDGE,"E50.0")])]})])],"derivedFrom":makeQuery(id+"F2.opExtrude","CAP_FACE",FACE,{"disambiguationData":[OSD([sQuery(id+"F0.wireOp",EDGE,"E1.left"),sQuery(id+"F0.wireOp",EDGE,"E3.bottom"),sQuery(id+"F0.wireOp",EDGE,"E3.top"),sQuery(id+"F0.wireOp",EDGE,"E3.left"),sQuery(id+"F0.wireOp",EDGE,"E3.right"),sQuery(id+"F0.wireOp",EDGE,"E4"),sQuery(id+"F0.wireOp",EDGE,"E5"),sQuery(id+"F0.wireOp",EDGE,"E6"),sQuery(id+"F0.wireOp",EDGE,"E7"),sQuery(id+"F0.wireOp",EDGE,"E8"),sQuery(id+"F0.wireOp",EDGE,"E9"),sQuery(id+"F0.wireOp",EDGE,"E10.trimOffspring"),sQuery(id+"F0.wireOp",EDGE,"E11.trimOffspring"),sQuery(id+"F0.wireOp",EDGE,"E12.trimOffspring")])],"isStart":true})});
            var Q1;
            Q1=makeQuery(id+"F7.boolean.opBoolean","SPLIT",FACE,{"disambiguationData":[TD([makeQuery(id+"F7.opExtrude","SWEPT_FACE",FACE,{"disambiguationData":[OSD([sQuery(id+"F6.wireOp",EDGE,"E51.MirrorCS")])]})])],"derivedFrom":makeQuery(id+"F2.opExtrude","CAP_FACE",FACE,{"disambiguationData":[OSD([sQuery(id+"F0.wireOp",EDGE,"E1.left"),sQuery(id+"F0.wireOp",EDGE,"E3.bottom"),sQuery(id+"F0.wireOp",EDGE,"E3.top"),sQuery(id+"F0.wireOp",EDGE,"E3.left"),sQuery(id+"F0.wireOp",EDGE,"E3.right"),sQuery(id+"F0.wireOp",EDGE,"E4"),sQuery(id+"F0.wireOp",EDGE,"E5"),sQuery(id+"F0.wireOp",EDGE,"E6"),sQuery(id+"F0.wireOp",EDGE,"E7"),sQuery(id+"F0.wireOp",EDGE,"E8"),sQuery(id+"F0.wireOp",EDGE,"E9"),sQuery(id+"F0.wireOp",EDGE,"E10.trimOffspring"),sQuery(id+"F0.wireOp",EDGE,"E11.trimOffspring"),sQuery(id+"F0.wireOp",EDGE,"E12.trimOffspring")])],"isStart":true})});
            var Q2;
            Q2=makeQuery(id+"F7.boolean.opBoolean","SPLIT",FACE,{"disambiguationData":[TD([makeQuery(id+"F7.opExtrude","SWEPT_FACE",FACE,{"disambiguationData":[OSD([sQuery(id+"F6.wireOp",EDGE,"E49.0")])]})])],"derivedFrom":makeQuery(id+"F2.opExtrude","CAP_FACE",FACE,{"disambiguationData":[OSD([sQuery(id+"F0.wireOp",EDGE,"E1.left"),sQuery(id+"F0.wireOp",EDGE,"E3.bottom"),sQuery(id+"F0.wireOp",EDGE,"E3.top"),sQuery(id+"F0.wireOp",EDGE,"E3.left"),sQuery(id+"F0.wireOp",EDGE,"E3.right"),sQuery(id+"F0.wireOp",EDGE,"E4"),sQuery(id+"F0.wireOp",EDGE,"E5"),sQuery(id+"F0.wireOp",EDGE,"E6"),sQuery(id+"F0.wireOp",EDGE,"E7"),sQuery(id+"F0.wireOp",EDGE,"E8"),sQuery(id+"F0.wireOp",EDGE,"E9"),sQuery(id+"F0.wireOp",EDGE,"E10.trimOffspring"),sQuery(id+"F0.wireOp",EDGE,"E11.trimOffspring"),sQuery(id+"F0.wireOp",EDGE,"E12.trimOffspring")])],"isStart":true})});
            var Q3;
            Q3=makeQuery(id+"F7.boolean.opBoolean","SPLIT",FACE,{"disambiguationData":[TD([makeQuery(id+"F7.opExtrude","SWEPT_FACE",FACE,{"disambiguationData":[OSD([sQuery(id+"F6.wireOp",EDGE,"E57.MirrorCS")])]})])],"derivedFrom":makeQuery(id+"F2.opExtrude","CAP_FACE",FACE,{"disambiguationData":[OSD([sQuery(id+"F0.wireOp",EDGE,"E1.left"),sQuery(id+"F0.wireOp",EDGE,"E3.bottom"),sQuery(id+"F0.wireOp",EDGE,"E3.top"),sQuery(id+"F0.wireOp",EDGE,"E3.left"),sQuery(id+"F0.wireOp",EDGE,"E3.right"),sQuery(id+"F0.wireOp",EDGE,"E4"),sQuery(id+"F0.wireOp",EDGE,"E5"),sQuery(id+"F0.wireOp",EDGE,"E6"),sQuery(id+"F0.wireOp",EDGE,"E7"),sQuery(id+"F0.wireOp",EDGE,"E8"),sQuery(id+"F0.wireOp",EDGE,"E9"),sQuery(id+"F0.wireOp",EDGE,"E10.trimOffspring"),sQuery(id+"F0.wireOp",EDGE,"E11.trimOffspring"),sQuery(id+"F0.wireOp",EDGE,"E12.trimOffspring")])],"isStart":true})});
            var Q4;
            Q4=makeQuery(id+"F7.boolean.opBoolean","SPLIT",FACE,{"disambiguationData":[TD([makeQuery(id+"F7.opExtrude","SWEPT_FACE",FACE,{"disambiguationData":[OSD([sQuery(id+"F6.wireOp",EDGE,"E48.0")])]})])],"derivedFrom":makeQuery(id+"F2.opExtrude","CAP_FACE",FACE,{"disambiguationData":[OSD([sQuery(id+"F0.wireOp",EDGE,"E1.left"),sQuery(id+"F0.wireOp",EDGE,"E3.bottom"),sQuery(id+"F0.wireOp",EDGE,"E3.top"),sQuery(id+"F0.wireOp",EDGE,"E3.left"),sQuery(id+"F0.wireOp",EDGE,"E3.right"),sQuery(id+"F0.wireOp",EDGE,"E4"),sQuery(id+"F0.wireOp",EDGE,"E5"),sQuery(id+"F0.wireOp",EDGE,"E6"),sQuery(id+"F0.wireOp",EDGE,"E7"),sQuery(id+"F0.wireOp",EDGE,"E8"),sQuery(id+"F0.wireOp",EDGE,"E9"),sQuery(id+"F0.wireOp",EDGE,"E10.trimOffspring"),sQuery(id+"F0.wireOp",EDGE,"E11.trimOffspring"),sQuery(id+"F0.wireOp",EDGE,"E12.trimOffspring")])],"isStart":true})});
            var Q5;
            Q5=makeQuery(id+"F7.boolean.opBoolean","SPLIT",FACE,{"disambiguationData":[TD([makeQuery(id+"F7.opExtrude","SWEPT_FACE",FACE,{"disambiguationData":[OSD([sQuery(id+"F6.wireOp",EDGE,"E64.MirrorCS")])]})])],"derivedFrom":makeQuery(id+"F2.opExtrude","CAP_FACE",FACE,{"disambiguationData":[OSD([sQuery(id+"F0.wireOp",EDGE,"E1.left"),sQuery(id+"F0.wireOp",EDGE,"E3.bottom"),sQuery(id+"F0.wireOp",EDGE,"E3.top"),sQuery(id+"F0.wireOp",EDGE,"E3.left"),sQuery(id+"F0.wireOp",EDGE,"E3.right"),sQuery(id+"F0.wireOp",EDGE,"E4"),sQuery(id+"F0.wireOp",EDGE,"E5"),sQuery(id+"F0.wireOp",EDGE,"E6"),sQuery(id+"F0.wireOp",EDGE,"E7"),sQuery(id+"F0.wireOp",EDGE,"E8"),sQuery(id+"F0.wireOp",EDGE,"E9"),sQuery(id+"F0.wireOp",EDGE,"E10.trimOffspring"),sQuery(id+"F0.wireOp",EDGE,"E11.trimOffspring"),sQuery(id+"F0.wireOp",EDGE,"E12.trimOffspring")])],"isStart":true})});
            var Q6;
            Q6=makeQuery(id+"F7.boolean.opBoolean","COPY",EDGE,{"derivedFrom":makeQuery(id+"F7.opExtrude","CAP_EDGE",EDGE,{"disambiguationData":[OSD([sQuery(id+"F6.wireOp",EDGE,"E45.top")])],"isStart":true})});
            var Q7;
            Q7=makeQuery(id+"F7.boolean.opBoolean","COPY",EDGE,{"derivedFrom":makeQuery(id+"F7.opExtrude","CAP_EDGE",EDGE,{"disambiguationData":[OSD([sQuery(id+"F6.wireOp",EDGE,"E45.left")])],"isStart":true})});
            var Q8;
            Q8=makeQuery(id+"F7.boolean.opBoolean","COPY",EDGE,{"derivedFrom":makeQuery(id+"F7.opExtrude","CAP_EDGE",EDGE,{"disambiguationData":[OSD([sQuery(id+"F6.wireOp",EDGE,"E45.bottom")])],"isStart":true})});
            var Q9;
            Q9=makeQuery(id+"F7.boolean.opBoolean","COPY",EDGE,{"derivedFrom":makeQuery(id+"F7.opExtrude","CAP_EDGE",EDGE,{"disambiguationData":[OSD([sQuery(id+"F6.wireOp",EDGE,"E45.right")])],"isStart":true})});
            var Q10;
            Q10=makeQuery(id+"F7.boolean.opBoolean","COPY",EDGE,{"derivedFrom":makeQuery(id+"F7.opExtrude","CAP_EDGE",EDGE,{"disambiguationData":[OSD([sQuery(id+"F6.wireOp",EDGE,"E53.MirrorCS")])],"isStart":true})});
            var Q11;
            Q11=makeQuery(id+"F7.boolean.opBoolean","COPY",EDGE,{"derivedFrom":makeQuery(id+"F7.opExtrude","CAP_EDGE",EDGE,{"disambiguationData":[OSD([sQuery(id+"F6.wireOp",EDGE,"E54.MirrorCS")])],"isStart":true})});
            var Q12;
            Q12=makeQuery(id+"F7.boolean.opBoolean","COPY",EDGE,{"derivedFrom":makeQuery(id+"F7.opExtrude","CAP_EDGE",EDGE,{"disambiguationData":[OSD([sQuery(id+"F6.wireOp",EDGE,"E66.MirrorCS")])],"isStart":true})});
            var Q13;
            Q13=makeQuery(id+"F7.boolean.opBoolean","COPY",EDGE,{"derivedFrom":makeQuery(id+"F7.opExtrude","CAP_EDGE",EDGE,{"disambiguationData":[OSD([sQuery(id+"F6.wireOp",EDGE,"E55.MirrorCS")])],"isStart":true})});
            var Q14;
            Q14=makeQuery(id+"F7.boolean.opBoolean","COPY",EDGE,{"derivedFrom":makeQuery(id+"F7.opExtrude","CAP_EDGE",EDGE,{"disambiguationData":[OSD([sQuery(id+"F6.wireOp",EDGE,"E46.bottom")])],"isStart":true})});
            var Q15;
            Q15=makeQuery(id+"F7.boolean.opBoolean","COPY",EDGE,{"derivedFrom":makeQuery(id+"F7.opExtrude","CAP_EDGE",EDGE,{"disambiguationData":[OSD([sQuery(id+"F6.wireOp",EDGE,"E46.right")])],"isStart":true})});
            var Q16;
            Q16=makeQuery(id+"F7.boolean.opBoolean","COPY",EDGE,{"derivedFrom":makeQuery(id+"F7.opExtrude","CAP_EDGE",EDGE,{"disambiguationData":[OSD([sQuery(id+"F6.wireOp",EDGE,"E46.left")])],"isStart":true})});
            var Q17;
            Q17=makeQuery(id+"F7.boolean.opBoolean","COPY",EDGE,{"derivedFrom":makeQuery(id+"F7.opExtrude","CAP_EDGE",EDGE,{"disambiguationData":[OSD([sQuery(id+"F6.wireOp",EDGE,"E59.MirrorCS")])],"isStart":true})});
            var Q18;
            Q18=makeQuery(id+"F7.boolean.opBoolean","COPY",EDGE,{"derivedFrom":makeQuery(id+"F7.opExtrude","CAP_EDGE",EDGE,{"disambiguationData":[OSD([sQuery(id+"F6.wireOp",EDGE,"E72.MirrorCS")])],"isStart":true})});
            var Q19;
            Q19=makeQuery(id+"F7.boolean.opBoolean","COPY",EDGE,{"derivedFrom":makeQuery(id+"F7.opExtrude","CAP_EDGE",EDGE,{"disambiguationData":[OSD([sQuery(id+"F6.wireOp",EDGE,"E56.MirrorCS")])],"isStart":true})});
            var Q20;
            Q20=makeQuery(id+"F7.boolean.opBoolean","COPY",EDGE,{"derivedFrom":makeQuery(id+"F7.opExtrude","CAP_EDGE",EDGE,{"disambiguationData":[OSD([sQuery(id+"F6.wireOp",EDGE,"E62.MirrorCS")])],"isStart":true})});
            var Q21;
            Q21=makeQuery(id+"F7.boolean.opBoolean","COPY",EDGE,{"derivedFrom":makeQuery(id+"F7.opExtrude","CAP_EDGE",EDGE,{"disambiguationData":[OSD([sQuery(id+"F6.wireOp",EDGE,"E46.top")])],"isStart":true})});
            var Q22;
            Q22=makeQuery(id+"F7.boolean.opBoolean","COPY",EDGE,{"derivedFrom":makeQuery(id+"F7.opExtrude","CAP_EDGE",EDGE,{"disambiguationData":[OSD([sQuery(id+"F6.wireOp",EDGE,"E47.bottom")])],"isStart":true})});
            var Q23;
            Q23=makeQuery(id+"F7.boolean.opBoolean","COPY",EDGE,{"derivedFrom":makeQuery(id+"F7.opExtrude","CAP_EDGE",EDGE,{"disambiguationData":[OSD([sQuery(id+"F6.wireOp",EDGE,"E47.left")])],"isStart":true})});
            var Q24;
            Q24=makeQuery(id+"F7.boolean.opBoolean","COPY",EDGE,{"derivedFrom":makeQuery(id+"F7.opExtrude","CAP_EDGE",EDGE,{"disambiguationData":[OSD([sQuery(id+"F6.wireOp",EDGE,"E47.right")])],"isStart":true})});
            var Q25;
            Q25=makeQuery(id+"F7.boolean.opBoolean","COPY",EDGE,{"derivedFrom":makeQuery(id+"F7.opExtrude","CAP_EDGE",EDGE,{"disambiguationData":[OSD([sQuery(id+"F6.wireOp",EDGE,"E73.MirrorCS")])],"isStart":true})});
            var Q26;
            Q26=makeQuery(id+"F7.boolean.opBoolean","COPY",EDGE,{"derivedFrom":makeQuery(id+"F7.opExtrude","CAP_EDGE",EDGE,{"disambiguationData":[OSD([sQuery(id+"F6.wireOp",EDGE,"E67.MirrorCS")])],"isStart":true})});
            var Q27;
            Q27=makeQuery(id+"F7.boolean.opBoolean","COPY",EDGE,{"derivedFrom":makeQuery(id+"F7.opExtrude","CAP_EDGE",EDGE,{"disambiguationData":[OSD([sQuery(id+"F6.wireOp",EDGE,"E71.MirrorCS")])],"isStart":true})});
            var Q28;
            Q28=makeQuery(id+"F7.boolean.opBoolean","COPY",EDGE,{"derivedFrom":makeQuery(id+"F7.opExtrude","CAP_EDGE",EDGE,{"disambiguationData":[OSD([sQuery(id+"F6.wireOp",EDGE,"E60.MirrorCS")])],"isStart":true})});
            var Q29;
            Q29=makeQuery(id+"F7.boolean.opBoolean","COPY",EDGE,{"derivedFrom":makeQuery(id+"F7.opExtrude","CAP_EDGE",EDGE,{"disambiguationData":[OSD([sQuery(id+"F6.wireOp",EDGE,"E47.top")])],"isStart":true})});
            chamfer(context, id + "F8", {"entities" : qUnion([Q0, Q1, Q2, Q3, Q4, Q5, Q6, Q7, Q8, Q9, Q10, Q11, Q12, Q13, Q14, Q15, Q16, Q17, Q18, Q19, Q20, Q21, Q22, Q23, Q24, Q25, Q26, Q27, Q28, Q29]), "width" : 12.7 * mm, "tangentPropagation" : true});
        }
        {
            var Q0;
            {var subQ0=sQuery(id+"F0.wireOp",EDGE,"E12.trimOffspring");var subQ1=sQuery(id+"F0.wireOp",EDGE,"E11.trimOffspring");var subQ2=sQuery(id+"F0.wireOp",EDGE,"E10.trimOffspring");var subQ3=sQuery(id+"F0.wireOp",EDGE,"E7");var subQ4=sQuery(id+"F0.wireOp",EDGE,"E6");var subQ5=sQuery(id+"F0.wireOp",EDGE,"E5");var subQ6=sQuery(id+"F0.wireOp",EDGE,"E4");var subQ7=sQuery(id+"F0.wireOp",EDGE,"E9");var subQ8=sQuery(id+"F0.wireOp",EDGE,"E3.left");var subQ9=sQuery(id+"F0.wireOp",EDGE,"E3.bottom");var subQ10=sQuery(id+"F0.wireOp",EDGE,"E3.top");var subQ11=sQuery(id+"F0.wireOp",EDGE,"E1.left");var subQ12=sQuery(id+"F0.wireOp",EDGE,"E3.right");var subQ13=sQuery(id+"F0.wireOp",EDGE,"E8");Q0=makeQuery(id+"F4.boolean.opBoolean","SPLIT",FACE,{"disambiguationData":[TD([makeQuery(id+"F1.opExtrude","SWEPT_FACE",FACE,{"disambiguationData":[OSD([subQ11])]})])],"derivedFrom":makeQuery(id+"F2.opExtrude","CAP_FACE",FACE,{"disambiguationData":[OSD([subQ11,subQ9,subQ10,subQ8,subQ12,subQ6,subQ5,subQ4,subQ3,subQ13,subQ7,subQ2,subQ1,subQ0])],"isStart":false})});}
            var sketch = newSketch(context, id + "F9", { "sketchPlane" : qUnion([Q0])});
            skCircle(sketch, "E75", {"center": v(307.97, -114.3) * mm, "radius": 34.93 * mm});
            skSolve(sketch);
        }
        {
            var Q0;
            Q0=makeQuery(id+"F9.imprint","IMPRINT",FACE,{"disambiguationData":[TD([[makeQuery(id+"F9.imprint","IMPRINT",EDGE,{"derivedFrom":sQuery(id+"F9.wireOp",EDGE,"E75")}),1.0]])]});
            extrude(context, id + "F10", {"entities" : qUnion([Q0]), "operationType" : NewBodyOperationType.ADD, "depth" : 12.7 * mm, "offsetDistance" : 25.4 * mm});
        }
        {
            var Q0;
            Q0=makeQuery(id+"F10.opExtrude","CAP_FACE",FACE,{"disambiguationData":[OSD([sQuery(id+"F9.wireOp",EDGE,"E75")])],"isStart":false});
            chamfer(context, id + "F11", {"entities" : qUnion([Q0]), "width" : 12.7 * mm, "tangentPropagation" : true});
        }
        {
            var Q0;
            Q0=makeQuery(id+"F10.opExtrude","CAP_FACE",FACE,{"disambiguationData":[OSD([sQuery(id+"F9.wireOp",EDGE,"E75")])],"isStart":false});
            var sketch = newSketch(context, id + "F12", { "sketchPlane" : qUnion([Q0])});
            skCircle(sketch, "E76", {"center": v(307.97, -114.3) * mm, "radius": 9.53 * mm});
            skSolve(sketch);
        }
        {
            var Q0;
            Q0 = qSketchRegion(id + "F12", true);
            extrude(context, id + "F13", {"entities" : qUnion([Q0]), "operationType" : NewBodyOperationType.ADD, "depth" : 12.7 * mm, "offsetDistance" : 25.4 * mm});
        }
        {
            var Q0;
            Q0=makeQuery(id+"F13.opExtrude","CAP_FACE",FACE,{"disambiguationData":[OSD([sQuery(id+"F12.wireOp",EDGE,"E76")])],"isStart":false});
            var sketch = newSketch(context, id + "F14", { "sketchPlane" : qUnion([Q0])});
            skCircle(sketch, "E77", {"center": v(307.97, -114.3) * mm, "radius": 31.75 * mm});
            skSolve(sketch);
        }
        {
            var Q0;
            Q0=makeQuery(id+"F14.imprint","IMPRINT",FACE,{"disambiguationData":[TD([[makeQuery(id+"F14.imprint","IMPRINT",EDGE,{"derivedFrom":sQuery(id+"F14.wireOp",EDGE,"E77")}),1.0]])]});
            var Q1;
            Q1=makeQuery(id+"F14.imprint","IMPRINT",FACE,{"disambiguationData":[TD([[makeQuery(id+"F14.imprint","IMPRINT",EDGE,{"derivedFrom":makeQuery(id+"F13.opExtrude","CAP_EDGE",EDGE,{"disambiguationData":[OSD([sQuery(id+"F12.wireOp",EDGE,"E76")])],"isStart":false})}),1.0]])]});
            extrude(context, id + "F15", {"entities" : qUnion([Q0, Q1]), "operationType" : NewBodyOperationType.ADD, "depth" : 25.4 * mm, "offsetDistance" : 25.4 * mm});
        }
        {
            var Q0;
            Q0=makeQuery(id+"F15.opExtrude","SWEPT_FACE",FACE,{"disambiguationData":[OSD([sQuery(id+"F14.wireOp",EDGE,"E77")])]});
            fillet(context, id + "F16", {"entities" : qUnion([Q0]), "radius" : 12.7 * mm, "tangentPropagation" : true, "allowEdgeOverflow" : false});
        }
        {
            var Q0;
            {var subQ0=sQuery(id+"F0.wireOp",EDGE,"E12.trimOffspring");var subQ1=sQuery(id+"F0.wireOp",EDGE,"E11.trimOffspring");var subQ2=sQuery(id+"F0.wireOp",EDGE,"E10.trimOffspring");var subQ3=sQuery(id+"F0.wireOp",EDGE,"E9");var subQ4=sQuery(id+"F0.wireOp",EDGE,"E3.left");var subQ5=sQuery(id+"F0.wireOp",EDGE,"E3.bottom");var subQ6=sQuery(id+"F0.wireOp",EDGE,"E3.top");var subQ7=sQuery(id+"F0.wireOp",EDGE,"E1.left");var subQ8=sQuery(id+"F0.wireOp",EDGE,"E3.right");var subQ9=sQuery(id+"F0.wireOp",EDGE,"E4");var subQ10=sQuery(id+"F0.wireOp",EDGE,"E5");var subQ11=sQuery(id+"F0.wireOp",EDGE,"E6");var subQ12=sQuery(id+"F0.wireOp",EDGE,"E7");var subQ13=sQuery(id+"F0.wireOp",EDGE,"E8");Q0=makeQuery(id+"F7.boolean.opBoolean","SPLIT",FACE,{"disambiguationData":[TD([makeQuery(id+"F1.opExtrude","SWEPT_FACE",FACE,{"disambiguationData":[OSD([subQ7])]})])],"derivedFrom":makeQuery(id+"F2.opExtrude","CAP_FACE",FACE,{"disambiguationData":[OSD([subQ7,subQ5,subQ6,subQ4,subQ8,subQ9,subQ10,subQ11,subQ12,subQ13,subQ3,subQ2,subQ1,subQ0])],"isStart":true})});}
            var sketch = newSketch(context, id + "F17", { "sketchPlane" : qUnion([Q0])});
            skCircle(sketch, "E78", {"center": v(-307.97, -101.6) * mm, "radius": 34.93 * mm});
            skSolve(sketch);
        }
        {
            var Q0;
            Q0=makeQuery(id+"F17.imprint","IMPRINT",FACE,{"disambiguationData":[TD([[makeQuery(id+"F17.imprint","IMPRINT",EDGE,{"derivedFrom":sQuery(id+"F17.wireOp",EDGE,"E78")}),1.0]])]});
            extrude(context, id + "F18", {"entities" : qUnion([Q0]), "operationType" : NewBodyOperationType.ADD, "depth" : 12.7 * mm, "offsetDistance" : 25.4 * mm});
        }
        {
            var Q0;
            Q0=makeQuery(id+"F18.opExtrude","CAP_FACE",FACE,{"disambiguationData":[OSD([sQuery(id+"F17.wireOp",EDGE,"E78")])],"isStart":false});
            chamfer(context, id + "F19", {"entities" : qUnion([Q0]), "width" : 12.7 * mm, "tangentPropagation" : true});
        }
        {
            var Q0;
            Q0=makeQuery(id+"F18.opExtrude","CAP_FACE",FACE,{"disambiguationData":[OSD([sQuery(id+"F17.wireOp",EDGE,"E78")])],"isStart":false});
            var sketch = newSketch(context, id + "F20", { "sketchPlane" : qUnion([Q0])});
            skCircle(sketch, "E79", {"center": v(-307.97, -101.6) * mm, "radius": 9.53 * mm});
            skSolve(sketch);
        }
        {
            var Q0;
            Q0=makeQuery(id+"F20.imprint","IMPRINT",FACE,{"disambiguationData":[TD([[makeQuery(id+"F20.imprint","IMPRINT",EDGE,{"derivedFrom":sQuery(id+"F20.wireOp",EDGE,"E79")}),1.0]])]});
            extrude(context, id + "F21", {"entities" : qUnion([Q0]), "operationType" : NewBodyOperationType.ADD, "depth" : 12.7 * mm, "offsetDistance" : 25.4 * mm});
        }
        {
            var Q0;
            Q0=makeQuery(id+"F21.opExtrude","CAP_FACE",FACE,{"disambiguationData":[OSD([sQuery(id+"F20.wireOp",EDGE,"E79")])],"isStart":false});
            var sketch = newSketch(context, id + "F22", { "sketchPlane" : qUnion([Q0])});
            skCircle(sketch, "E80", {"center": v(-307.97, -101.6) * mm, "radius": 31.75 * mm});
            skSolve(sketch);
        }
        {
            var Q0;
            Q0=makeQuery(id+"F22.imprint","IMPRINT",FACE,{"disambiguationData":[TD([[makeQuery(id+"F22.imprint","IMPRINT",EDGE,{"derivedFrom":sQuery(id+"F22.wireOp",EDGE,"E80")}),1.0]])]});
            var Q1;
            Q1=makeQuery(id+"F22.imprint","IMPRINT",FACE,{"disambiguationData":[TD([[makeQuery(id+"F22.imprint","IMPRINT",EDGE,{"derivedFrom":makeQuery(id+"F21.opExtrude","CAP_EDGE",EDGE,{"disambiguationData":[OSD([sQuery(id+"F20.wireOp",EDGE,"E79")])],"isStart":false})}),1.0]])]});
            extrude(context, id + "F23", {"entities" : qUnion([Q0, Q1]), "operationType" : NewBodyOperationType.ADD, "depth" : 25.4 * mm, "offsetDistance" : 25.4 * mm});
        }
        {
            var Q0;
            Q0=makeQuery(id+"F23.opExtrude","SWEPT_FACE",FACE,{"disambiguationData":[OSD([sQuery(id+"F22.wireOp",EDGE,"E80")])]});
            fillet(context, id + "F24", {"entities" : qUnion([Q0]), "radius" : 12.7 * mm, "tangentPropagation" : true, "allowEdgeOverflow" : false});
        }
    });
